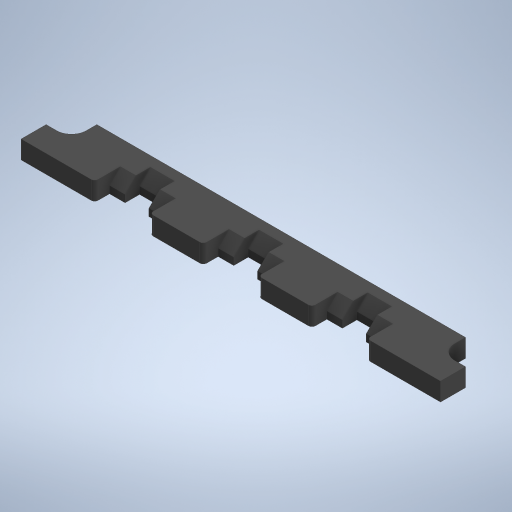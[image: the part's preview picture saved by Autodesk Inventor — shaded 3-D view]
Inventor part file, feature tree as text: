
AUTODESK INVENTOR PART (.ipt)
format: ipt  version: 2024 (Build 280153000, 153)  size: 416,256 bytes
history: native  units: mm
features: extrude x3, sketch x3, chamfer x2, fillet x1, projected_geometry x1
ambient origin geometry x8: Origin, YZ Plane, XZ Plane, XY Plane, X Axis, Y Axis, Z Axis, Center Point
bodies: Solide1 (feature_tree)
feature tree (10):
  extrude  "Extrusion1"  Depth=5.0mm TaperAngle=0.0deg
  extrude  "Extrusion2"  Depth=0.1mm
  chamfer  "Chanfrein1"  Distance=5.0mm
  fillet  "Congé1"  Radius=3.0mm
  extrude  "Extrusion3"  Depth=1.0mm
  chamfer  "Chanfrein2"  Distance=6.6mm
  sketch  "Esquisse1"
  sketch  "Esquisse2"
  projected_geometry  "Boucle projetée1"
  sketch  "Esquisse4"
